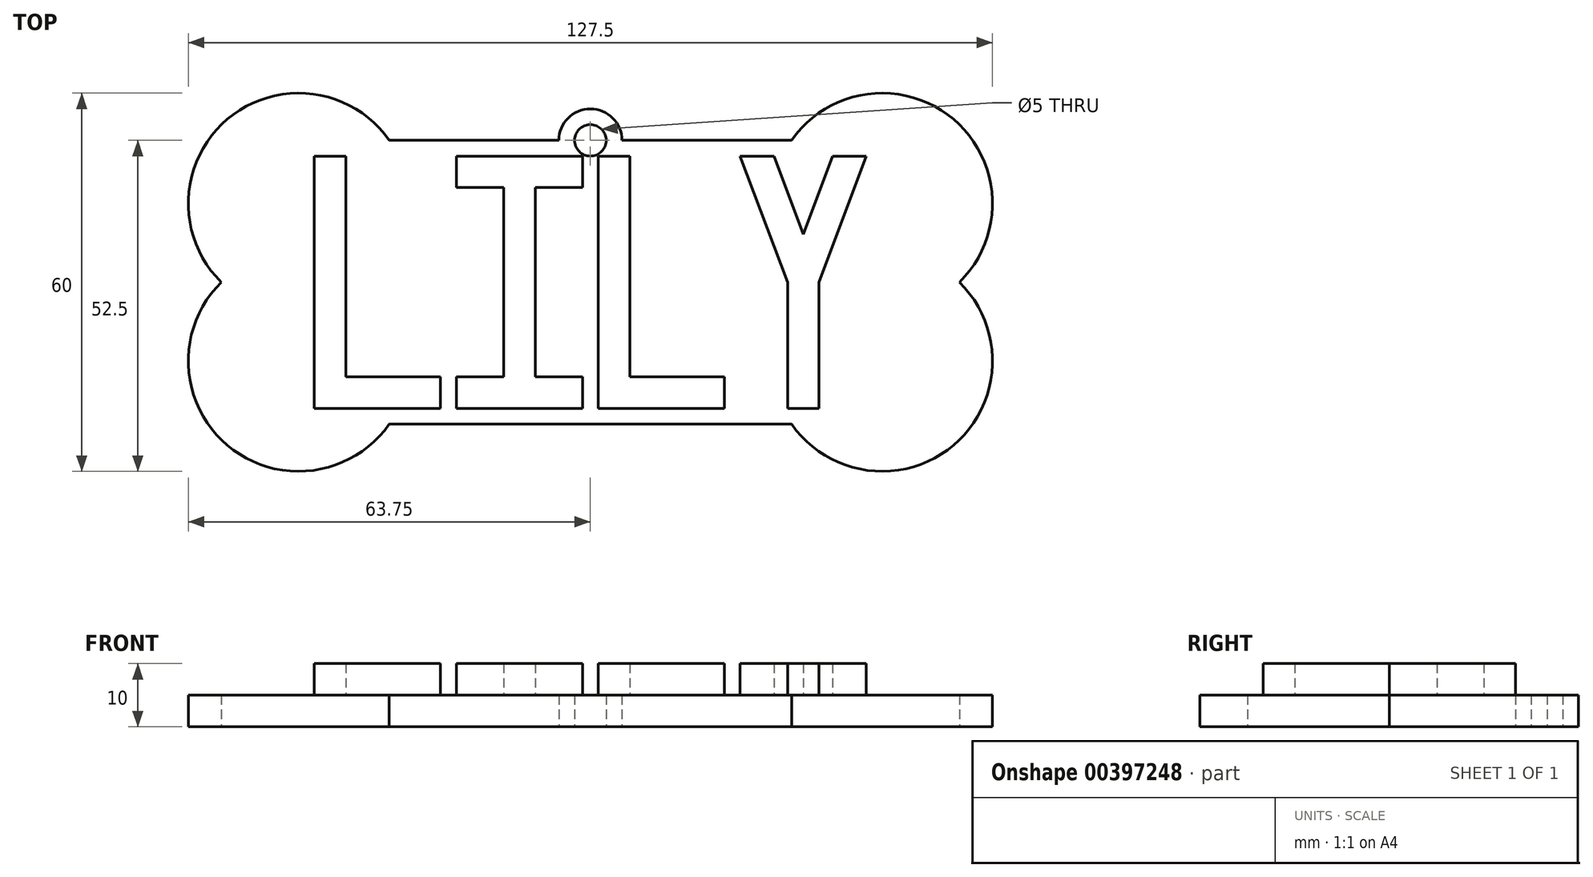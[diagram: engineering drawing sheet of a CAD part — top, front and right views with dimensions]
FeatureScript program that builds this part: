
annotation { "Feature Type Name" : "Feature", "Feature Type Description" : "" }
export const myFeature = defineFeature(function(context is Context, id is Id, definition is map)
    precondition{}
    {
        {
            var Q0;
            Q0=qCreatedBy(makeId("Top.planeOp"),FACE);
            var sketch = newSketch(context, id + "F0", { "sketchPlane" : qUnion([Q0])});
            skLineSegment(sketch, "E0.bottom", {"start": v(-90, 42.5) * mm, "end": v(-70, 42.5) * mm});
            skLineSegment(sketch, "E0.top", {"start": v(-90, 2.5) * mm, "end": v(-70, 2.5) * mm});
            skLineSegment(sketch, "E0.left", {"start": v(-90, 42.5) * mm, "end": v(-90, 2.5) * mm});
            skLineSegment(sketch, "E0.right", {"start": v(-70, 42.5) * mm, "end": v(-70, 2.5) * mm});
            skLineSegment(sketch, "E1", {"start": v(-85, 42.5) * mm, "end": v(-85, 2.5) * mm});
            skLineSegment(sketch, "E2", {"start": v(-90, 7.5) * mm, "end": v(-70, 7.5) * mm});
            skLineSegment(sketch, "E3.bottom", {"start": v(-67.5, 42.5) * mm, "end": v(-47.5, 42.5) * mm});
            skLineSegment(sketch, "E3.top", {"start": v(-67.5, 2.5) * mm, "end": v(-47.5, 2.5) * mm});
            skLineSegment(sketch, "E3.left", {"start": v(-67.5, 42.5) * mm, "end": v(-67.5, 2.5) * mm});
            skLineSegment(sketch, "E3.right", {"start": v(-47.5, 42.5) * mm, "end": v(-47.5, 2.5) * mm});
            skLineSegment(sketch, "E4.bottom", {"start": v(-22.5, 42.5) * mm, "end": v(-2.5, 42.5) * mm});
            skLineSegment(sketch, "E4.top", {"start": v(-22.5, 2.5) * mm, "end": v(-2.5, 2.5) * mm});
            skLineSegment(sketch, "E4.left", {"start": v(-22.5, 42.5) * mm, "end": v(-22.5, 2.5) * mm});
            skLineSegment(sketch, "E4.right", {"start": v(-2.5, 42.5) * mm, "end": v(-2.5, 2.5) * mm});
            skLineSegment(sketch, "E5", {"start": v(-67.5, 7.5) * mm, "end": v(-47.5, 7.5) * mm});
            skLineSegment(sketch, "E6", {"start": v(-22.5, 22.5) * mm, "end": v(-2.5, 22.5) * mm});
            skLineSegment(sketch, "E7", {"start": v(-15, 22.5) * mm, "end": v(-15, 2.5) * mm});
            skLineSegment(sketch, "E8", {"start": v(-10, 22.5) * mm, "end": v(-10, 2.5) * mm});
            skLineSegment(sketch, "E9", {"start": v(-10, 22.5) * mm, "end": v(-2.5, 42.5) * mm});
            skLineSegment(sketch, "E10", {"start": v(-15, 22.5) * mm, "end": v(-22.5, 42.5) * mm});
            skLineSegment(sketch, "E11", {"start": v(-17.16, 42.5) * mm, "end": v(-12.5, 30.07) * mm});
            skLineSegment(sketch, "E12", {"start": v(-12.5, 30.07) * mm, "end": v(-7.84, 42.5) * mm});
            skLineSegment(sketch, "E13.bottom", {"start": v(-92.5, 45) * mm, "end": v(0, 45) * mm});
            skLineSegment(sketch, "E13.top", {"start": v(-92.5, 0) * mm, "end": v(0, 0) * mm});
            skLineSegment(sketch, "E13.left", {"start": v(-92.5, 45) * mm, "end": v(-92.5, 0) * mm});
            skLineSegment(sketch, "E13.right", {"start": v(0, 45) * mm, "end": v(0, 0) * mm});
            skLineSegment(sketch, "E14", {"start": v(-67.5, 37.5) * mm, "end": v(-47.5, 37.5) * mm});
            skLineSegment(sketch, "E15", {"start": v(-60, 37.5) * mm, "end": v(-60, 7.5) * mm});
            skLineSegment(sketch, "E16", {"start": v(-55, 37.5) * mm, "end": v(-55, 7.5) * mm});
            skLineSegment(sketch, "E17.bottom", {"start": v(-45, 42.5) * mm, "end": v(-25, 42.5) * mm});
            skLineSegment(sketch, "E17.top", {"start": v(-45, 2.5) * mm, "end": v(-25, 2.5) * mm});
            skLineSegment(sketch, "E17.left", {"start": v(-45, 42.5) * mm, "end": v(-45, 2.5) * mm});
            skLineSegment(sketch, "E17.right", {"start": v(-25, 42.5) * mm, "end": v(-25, 2.5) * mm});
            skLineSegment(sketch, "E18", {"start": v(-40, 42.5) * mm, "end": v(-40, 2.5) * mm});
            skLineSegment(sketch, "E19", {"start": v(-45, 7.5) * mm, "end": v(-25, 7.5) * mm});
            skPoint(sketch, "E20", {"position": v(-92.5, 35) * mm});
            skPoint(sketch, "E21", {"position": v(-92.5, 10) * mm});
            skPoint(sketch, "E22", {"position": v(0, 10) * mm});
            skPoint(sketch, "E23", {"position": v(0, 35) * mm});
            skCircle(sketch, "E24", {"center": v(-92.5, 35) * mm, "radius": 17.5 * mm});
            skCircle(sketch, "E25", {"center": v(-92.5, 10) * mm, "radius": 17.5 * mm});
            skCircle(sketch, "E26", {"center": v(0, 35) * mm, "radius": 17.5 * mm});
            skCircle(sketch, "E27", {"center": v(0, 10) * mm, "radius": 17.5 * mm});
            skPoint(sketch, "E28", {"position": v(-46.25, 45) * mm});
            skCircle(sketch, "E29", {"center": v(-46.25, 45) * mm, "radius": 2.5 * mm});
            skCircle(sketch, "E30", {"center": v(-46.25, 45) * mm, "radius": 5 * mm});
            skSolve(sketch);
        }
        {
            var Q0;
            Q0 = qSketchRegion(id + "F0", true);
            var Q1;
            {var subQ1=sQuery(id+"F0.wireOp",EDGE,"E4.right");var subQ5=makeQuery(id+"F0.imprint","INTERSECT",VERTEX,{"derivedFrom":[subQ1,sQuery(id+"F0.wireOp",EDGE,"E6")]});Q1=makeQuery(id+"F0.imprint","IMPRINT",FACE,{"disambiguationData":[TD([[makeQuery(id+"F0.imprint","IMPRINT",EDGE,{"disambiguationData":[TD([[subQ5,1.0]])],"derivedFrom":subQ1}),1.0]])]});}
            var Q2;
            {var subQ0=sQuery(id+"F0.wireOp",EDGE,"E4.right");var subQ1=sQuery(id+"F0.wireOp",EDGE,"E4.top");var subQ2=makeQuery(id+"F0.imprint","INTERSECT",VERTEX,{"derivedFrom":[subQ1,subQ0]});Q2=makeQuery(id+"F0.imprint","IMPRINT",FACE,{"disambiguationData":[TD([[makeQuery(id+"F0.imprint","IMPRINT",EDGE,{"disambiguationData":[TD([[subQ2,1.0]])],"derivedFrom":subQ1}),1.0]])]});}
            var Q3;
            {var subQ0=sQuery(id+"F0.wireOp",EDGE,"E6");var subQ1=sQuery(id+"F0.wireOp",EDGE,"E4.right");var subQ2=makeQuery(id+"F0.imprint","INTERSECT",VERTEX,{"derivedFrom":[subQ1,subQ0]});Q3=makeQuery(id+"F0.imprint","IMPRINT",FACE,{"disambiguationData":[TD([[makeQuery(id+"F0.imprint","IMPRINT",EDGE,{"disambiguationData":[TD([[subQ2,-1.0]])],"derivedFrom":subQ1}),-1.0]])]});}
            var Q4;
            {var subQ1=sQuery(id+"F0.wireOp",EDGE,"E4.right");var subQ3=sQuery(id+"F0.wireOp",EDGE,"E27");var subQ4=makeQuery(id+"F0.imprint","INTERSECT",VERTEX,{"derivedFrom":[subQ1,subQ3]});Q4=makeQuery(id+"F0.imprint","IMPRINT",FACE,{"disambiguationData":[TD([[makeQuery(id+"F0.imprint","IMPRINT",EDGE,{"disambiguationData":[TD([[subQ4,-1.0]])],"derivedFrom":subQ3}),-1.0]])]});}
            var Q5;
            {var subQ0=sQuery(id+"F0.wireOp",EDGE,"E6");var subQ1=sQuery(id+"F0.wireOp",EDGE,"E4.right");var subQ2=makeQuery(id+"F0.imprint","INTERSECT",VERTEX,{"derivedFrom":[subQ1,subQ0]});Q5=makeQuery(id+"F0.imprint","IMPRINT",FACE,{"disambiguationData":[TD([[makeQuery(id+"F0.imprint","IMPRINT",EDGE,{"disambiguationData":[TD([[subQ2,1.0]])],"derivedFrom":subQ1}),-1.0]])]});}
            var Q6;
            {var subQ0=sQuery(id+"F0.wireOp",EDGE,"E9");var subQ3=sQuery(id+"F0.wireOp",EDGE,"E27");var subQ5=makeQuery(id+"F0.imprint","INTERSECT",VERTEX,{"derivedFrom":[subQ0,subQ3]});Q6=makeQuery(id+"F0.imprint","IMPRINT",FACE,{"disambiguationData":[TD([[makeQuery(id+"F0.imprint","IMPRINT",EDGE,{"disambiguationData":[TD([[subQ5,1.0]])],"derivedFrom":subQ0}),1.0]])]});}
            var Q7;
            {var subQ0=sQuery(id+"F0.wireOp",EDGE,"E8");var subQ3=sQuery(id+"F0.wireOp",EDGE,"E26");var subQ5=makeQuery(id+"F0.imprint","INTERSECT",VERTEX,{"derivedFrom":[subQ0,subQ3]});Q7=makeQuery(id+"F0.imprint","IMPRINT",FACE,{"disambiguationData":[TD([[makeQuery(id+"F0.imprint","IMPRINT",EDGE,{"disambiguationData":[TD([[subQ5,1.0]])],"derivedFrom":subQ0}),-1.0]])]});}
            var Q8;
            {var subQ5=sQuery(id+"F0.wireOp",EDGE,"E4.top");var subQ7=sQuery(id+"F0.wireOp",EDGE,"E7");var subQ8=makeQuery(id+"F0.imprint","INTERSECT",VERTEX,{"derivedFrom":[subQ5,subQ7]});Q8=makeQuery(id+"F0.imprint","IMPRINT",FACE,{"disambiguationData":[TD([[makeQuery(id+"F0.imprint","IMPRINT",EDGE,{"disambiguationData":[TD([[subQ8,-1.0]])],"derivedFrom":subQ5}),1.0]])]});}
            var Q9;
            {var subQ0=sQuery(id+"F0.wireOp",EDGE,"E7");var subQ3=sQuery(id+"F0.wireOp",EDGE,"E27");var subQ5=makeQuery(id+"F0.imprint","INTERSECT",VERTEX,{"derivedFrom":[subQ0,subQ3]});Q9=makeQuery(id+"F0.imprint","IMPRINT",FACE,{"disambiguationData":[TD([[makeQuery(id+"F0.imprint","IMPRINT",EDGE,{"disambiguationData":[TD([[subQ5,1.0]])],"derivedFrom":subQ0}),1.0]])]});}
            var Q10;
            {var subQ0=sQuery(id+"F0.wireOp",EDGE,"E7");var subQ1=sQuery(id+"F0.wireOp",EDGE,"E4.top");var subQ2=makeQuery(id+"F0.imprint","INTERSECT",VERTEX,{"derivedFrom":[subQ1,subQ0]});Q10=makeQuery(id+"F0.imprint","IMPRINT",FACE,{"disambiguationData":[TD([[makeQuery(id+"F0.imprint","IMPRINT",EDGE,{"disambiguationData":[TD([[subQ2,1.0]])],"derivedFrom":subQ1}),1.0]])]});}
            var Q11;
            {var subQ5=sQuery(id+"F0.wireOp",EDGE,"E4.left");var subQ7=sQuery(id+"F0.wireOp",EDGE,"E4.top");var subQ8=makeQuery(id+"F0.imprint","INTERSECT",VERTEX,{"derivedFrom":[subQ7,subQ5]});Q11=makeQuery(id+"F0.imprint","IMPRINT",FACE,{"disambiguationData":[TD([[makeQuery(id+"F0.imprint","IMPRINT",EDGE,{"disambiguationData":[TD([[subQ8,-1.0]])],"derivedFrom":subQ7}),1.0]])]});}
            var Q12;
            {var subQ0=sQuery(id+"F0.wireOp",EDGE,"E10");Q12=makeQuery(id+"F0.imprint","IMPRINT",FACE,{"disambiguationData":[TD([[makeQuery(id+"F0.imprint","IMPRINT",EDGE,{"derivedFrom":subQ0}),1.0]])]});}
            var Q13;
            {var subQ0=sQuery(id+"F0.wireOp",EDGE,"E12");Q13=makeQuery(id+"F0.imprint","IMPRINT",FACE,{"disambiguationData":[TD([[makeQuery(id+"F0.imprint","IMPRINT",EDGE,{"derivedFrom":subQ0}),-1.0]])]});}
            var Q14;
            {var subQ0=sQuery(id+"F0.wireOp",EDGE,"E10");Q14=makeQuery(id+"F0.imprint","IMPRINT",FACE,{"disambiguationData":[TD([[makeQuery(id+"F0.imprint","IMPRINT",EDGE,{"derivedFrom":subQ0}),-1.0]])]});}
            var Q15;
            {var subQ0=sQuery(id+"F0.wireOp",EDGE,"E12");Q15=makeQuery(id+"F0.imprint","IMPRINT",FACE,{"disambiguationData":[TD([[makeQuery(id+"F0.imprint","IMPRINT",EDGE,{"derivedFrom":subQ0}),1.0]])]});}
            var Q16;
            {var subQ0=sQuery(id+"F0.wireOp",EDGE,"E11");var subQ1=sQuery(id+"F0.wireOp",EDGE,"E4.bottom");var subQ2=makeQuery(id+"F0.imprint","INTERSECT",VERTEX,{"derivedFrom":[subQ1,subQ0]});Q16=makeQuery(id+"F0.imprint","IMPRINT",FACE,{"disambiguationData":[TD([[makeQuery(id+"F0.imprint","IMPRINT",EDGE,{"disambiguationData":[TD([[subQ2,-1.0]])],"derivedFrom":subQ1}),-1.0]])]});}
            var Q17;
            {var subQ0=sQuery(id+"F0.wireOp",EDGE,"E17.right");var subQ1=sQuery(id+"F0.wireOp",EDGE,"E17.bottom");var subQ2=makeQuery(id+"F0.imprint","INTERSECT",VERTEX,{"derivedFrom":[subQ1,subQ0]});Q17=makeQuery(id+"F0.imprint","IMPRINT",FACE,{"disambiguationData":[TD([[makeQuery(id+"F0.imprint","IMPRINT",EDGE,{"disambiguationData":[TD([[subQ2,1.0]])],"derivedFrom":subQ1}),-1.0]])]});}
            var Q18;
            {var subQ0=sQuery(id+"F0.wireOp",EDGE,"E17.left");var subQ1=sQuery(id+"F0.wireOp",EDGE,"E17.bottom");var subQ2=makeQuery(id+"F0.imprint","INTERSECT",VERTEX,{"derivedFrom":[subQ1,subQ0]});Q18=makeQuery(id+"F0.imprint","IMPRINT",FACE,{"disambiguationData":[TD([[makeQuery(id+"F0.imprint","IMPRINT",EDGE,{"disambiguationData":[TD([[subQ2,-1.0]])],"derivedFrom":subQ1}),-1.0]])]});}
            var Q19;
            {var subQ0=sQuery(id+"F0.wireOp",EDGE,"E17.left");var subQ1=sQuery(id+"F0.wireOp",EDGE,"E17.top");var subQ2=makeQuery(id+"F0.imprint","INTERSECT",VERTEX,{"derivedFrom":[subQ1,subQ0]});Q19=makeQuery(id+"F0.imprint","IMPRINT",FACE,{"disambiguationData":[TD([[makeQuery(id+"F0.imprint","IMPRINT",EDGE,{"disambiguationData":[TD([[subQ2,-1.0]])],"derivedFrom":subQ1}),1.0]])]});}
            var Q20;
            {var subQ0=sQuery(id+"F0.wireOp",EDGE,"E17.right");var subQ1=sQuery(id+"F0.wireOp",EDGE,"E17.top");var subQ2=makeQuery(id+"F0.imprint","INTERSECT",VERTEX,{"derivedFrom":[subQ1,subQ0]});Q20=makeQuery(id+"F0.imprint","IMPRINT",FACE,{"disambiguationData":[TD([[makeQuery(id+"F0.imprint","IMPRINT",EDGE,{"disambiguationData":[TD([[subQ2,1.0]])],"derivedFrom":subQ1}),1.0]])]});}
            var Q21;
            {var subQ5=sQuery(id+"F0.wireOp",EDGE,"E3.top");Q21=makeQuery(id+"F0.imprint","IMPRINT",FACE,{"disambiguationData":[TD([[makeQuery(id+"F0.imprint","IMPRINT",EDGE,{"derivedFrom":subQ5}),1.0]])]});}
            var Q22;
            {var subQ5=sQuery(id+"F0.wireOp",EDGE,"E16");Q22=makeQuery(id+"F0.imprint","IMPRINT",FACE,{"disambiguationData":[TD([[makeQuery(id+"F0.imprint","IMPRINT",EDGE,{"derivedFrom":subQ5}),1.0]])]});}
            var Q23;
            {var subQ0=sQuery(id+"F0.wireOp",EDGE,"E15");Q23=makeQuery(id+"F0.imprint","IMPRINT",FACE,{"disambiguationData":[TD([[makeQuery(id+"F0.imprint","IMPRINT",EDGE,{"derivedFrom":subQ0}),1.0]])]});}
            var Q24;
            {var subQ5=sQuery(id+"F0.wireOp",EDGE,"E15");Q24=makeQuery(id+"F0.imprint","IMPRINT",FACE,{"disambiguationData":[TD([[makeQuery(id+"F0.imprint","IMPRINT",EDGE,{"derivedFrom":subQ5}),-1.0]])]});}
            var Q25;
            {var subQ4=sQuery(id+"F0.wireOp",EDGE,"E3.bottom");Q25=makeQuery(id+"F0.imprint","IMPRINT",FACE,{"disambiguationData":[TD([[makeQuery(id+"F0.imprint","IMPRINT",EDGE,{"derivedFrom":subQ4}),-1.0]])]});}
            var Q26;
            {var subQ1=sQuery(id+"F0.wireOp",EDGE,"E0.bottom");var subQ6=sQuery(id+"F0.wireOp",EDGE,"E0.right");var subQ9=makeQuery(id+"F0.imprint","INTERSECT",VERTEX,{"derivedFrom":[subQ1,subQ6]});Q26=makeQuery(id+"F0.imprint","IMPRINT",FACE,{"disambiguationData":[TD([[makeQuery(id+"F0.imprint","IMPRINT",EDGE,{"disambiguationData":[TD([[subQ9,1.0]])],"derivedFrom":subQ1}),-1.0]])]});}
            var Q27;
            {var subQ0=sQuery(id+"F0.wireOp",EDGE,"E1");var subQ1=sQuery(id+"F0.wireOp",EDGE,"E0.bottom");var subQ2=makeQuery(id+"F0.imprint","INTERSECT",VERTEX,{"derivedFrom":[subQ1,subQ0]});Q27=makeQuery(id+"F0.imprint","IMPRINT",FACE,{"disambiguationData":[TD([[makeQuery(id+"F0.imprint","IMPRINT",EDGE,{"disambiguationData":[TD([[subQ2,-1.0]])],"derivedFrom":subQ1}),-1.0]])]});}
            var Q28;
            {var subQ0=sQuery(id+"F0.wireOp",EDGE,"E24");var subQ1=sQuery(id+"F0.wireOp",EDGE,"E1");var subQ2=makeQuery(id+"F0.imprint","INTERSECT",VERTEX,{"derivedFrom":[subQ1,subQ0]});Q28=makeQuery(id+"F0.imprint","IMPRINT",FACE,{"disambiguationData":[TD([[makeQuery(id+"F0.imprint","IMPRINT",EDGE,{"disambiguationData":[TD([[subQ2,-1.0]])],"derivedFrom":subQ1}),1.0]])]});}
            var Q29;
            {var subQ0=sQuery(id+"F0.wireOp",EDGE,"E25");var subQ1=sQuery(id+"F0.wireOp",EDGE,"E1");var subQ2=makeQuery(id+"F0.imprint","INTERSECT",VERTEX,{"derivedFrom":[subQ1,subQ0]});Q29=makeQuery(id+"F0.imprint","IMPRINT",FACE,{"disambiguationData":[TD([[makeQuery(id+"F0.imprint","IMPRINT",EDGE,{"disambiguationData":[TD([[subQ2,-1.0]])],"derivedFrom":subQ1}),1.0]])]});}
            var Q30;
            {var subQ0=sQuery(id+"F0.wireOp",EDGE,"E25");var subQ1=sQuery(id+"F0.wireOp",EDGE,"E0.left");var subQ2=makeQuery(id+"F0.imprint","INTERSECT",VERTEX,{"derivedFrom":[subQ1,subQ0]});Q30=makeQuery(id+"F0.imprint","IMPRINT",FACE,{"disambiguationData":[TD([[makeQuery(id+"F0.imprint","IMPRINT",EDGE,{"disambiguationData":[TD([[subQ2,-1.0]])],"derivedFrom":subQ1}),1.0]])]});}
            var Q31;
            {var subQ0=sQuery(id+"F0.wireOp",EDGE,"E0.left");var subQ1=sQuery(id+"F0.wireOp",EDGE,"E0.bottom");var subQ2=makeQuery(id+"F0.imprint","INTERSECT",VERTEX,{"derivedFrom":[subQ1,subQ0]});Q31=makeQuery(id+"F0.imprint","IMPRINT",FACE,{"disambiguationData":[TD([[makeQuery(id+"F0.imprint","IMPRINT",EDGE,{"disambiguationData":[TD([[subQ2,-1.0]])],"derivedFrom":subQ1}),-1.0]])]});}
            var Q32;
            {var subQ0=sQuery(id+"F0.wireOp",EDGE,"E25");var subQ1=sQuery(id+"F0.wireOp",EDGE,"E0.left");var subQ2=makeQuery(id+"F0.imprint","INTERSECT",VERTEX,{"derivedFrom":[subQ1,subQ0]});Q32=makeQuery(id+"F0.imprint","IMPRINT",FACE,{"disambiguationData":[TD([[makeQuery(id+"F0.imprint","IMPRINT",EDGE,{"disambiguationData":[TD([[subQ2,-1.0]])],"derivedFrom":subQ1}),-1.0]])]});}
            var Q33;
            {var subQ0=sQuery(id+"F0.wireOp",EDGE,"E2");var subQ1=sQuery(id+"F0.wireOp",EDGE,"E0.left");var subQ2=makeQuery(id+"F0.imprint","INTERSECT",VERTEX,{"derivedFrom":[subQ1,subQ0]});Q33=makeQuery(id+"F0.imprint","IMPRINT",FACE,{"disambiguationData":[TD([[makeQuery(id+"F0.imprint","IMPRINT",EDGE,{"disambiguationData":[TD([[subQ2,1.0]])],"derivedFrom":subQ1}),1.0]])]});}
            var Q34;
            {var subQ0=sQuery(id+"F0.wireOp",EDGE,"E0.left");var subQ1=sQuery(id+"F0.wireOp",EDGE,"E0.top");var subQ2=makeQuery(id+"F0.imprint","INTERSECT",VERTEX,{"derivedFrom":[subQ1,subQ0]});Q34=makeQuery(id+"F0.imprint","IMPRINT",FACE,{"disambiguationData":[TD([[makeQuery(id+"F0.imprint","IMPRINT",EDGE,{"disambiguationData":[TD([[subQ2,-1.0]])],"derivedFrom":subQ1}),1.0]])]});}
            var Q35;
            {var subQ0=sQuery(id+"F0.wireOp",EDGE,"E1");var subQ1=sQuery(id+"F0.wireOp",EDGE,"E0.top");var subQ2=makeQuery(id+"F0.imprint","INTERSECT",VERTEX,{"derivedFrom":[subQ1,subQ0]});Q35=makeQuery(id+"F0.imprint","IMPRINT",FACE,{"disambiguationData":[TD([[makeQuery(id+"F0.imprint","IMPRINT",EDGE,{"disambiguationData":[TD([[subQ2,-1.0]])],"derivedFrom":subQ1}),1.0]])]});}
            var Q36;
            {var subQ0=sQuery(id+"F0.wireOp",EDGE,"E0.right");var subQ1=sQuery(id+"F0.wireOp",EDGE,"E0.top");var subQ2=makeQuery(id+"F0.imprint","INTERSECT",VERTEX,{"derivedFrom":[subQ1,subQ0]});Q36=makeQuery(id+"F0.imprint","IMPRINT",FACE,{"disambiguationData":[TD([[makeQuery(id+"F0.imprint","IMPRINT",EDGE,{"disambiguationData":[TD([[subQ2,1.0]])],"derivedFrom":subQ1}),1.0]])]});}
            extrude(context, id + "F1", {"entities" : qUnion([Q0, Q1, Q2, Q3, Q4, Q5, Q6, Q7, Q8, Q9, Q10, Q11, Q12, Q13, Q14, Q15, Q16, Q17, Q18, Q19, Q20, Q21, Q22, Q23, Q24, Q25, Q26, Q27, Q28, Q29, Q30, Q31, Q32, Q33, Q34, Q35, Q36]), "depth" : 5 * mm});
        }
        {
            var Q0;
            {var subQ0=sQuery(id+"F0.wireOp",EDGE,"E0.left");var subQ1=sQuery(id+"F0.wireOp",EDGE,"E0.bottom");var subQ2=makeQuery(id+"F0.imprint","INTERSECT",VERTEX,{"derivedFrom":[subQ1,subQ0]});Q0=makeQuery(id+"F0.imprint","IMPRINT",FACE,{"disambiguationData":[TD([[makeQuery(id+"F0.imprint","IMPRINT",EDGE,{"disambiguationData":[TD([[subQ2,-1.0]])],"derivedFrom":subQ1}),-1.0]])]});}
            var Q1;
            {var subQ0=sQuery(id+"F0.wireOp",EDGE,"E25");var subQ1=sQuery(id+"F0.wireOp",EDGE,"E0.left");var subQ2=makeQuery(id+"F0.imprint","INTERSECT",VERTEX,{"derivedFrom":[subQ1,subQ0]});Q1=makeQuery(id+"F0.imprint","IMPRINT",FACE,{"disambiguationData":[TD([[makeQuery(id+"F0.imprint","IMPRINT",EDGE,{"disambiguationData":[TD([[subQ2,-1.0]])],"derivedFrom":subQ1}),1.0]])]});}
            var Q2;
            {var subQ0=sQuery(id+"F0.wireOp",EDGE,"E2");var subQ1=sQuery(id+"F0.wireOp",EDGE,"E0.left");var subQ2=makeQuery(id+"F0.imprint","INTERSECT",VERTEX,{"derivedFrom":[subQ1,subQ0]});Q2=makeQuery(id+"F0.imprint","IMPRINT",FACE,{"disambiguationData":[TD([[makeQuery(id+"F0.imprint","IMPRINT",EDGE,{"disambiguationData":[TD([[subQ2,1.0]])],"derivedFrom":subQ1}),1.0]])]});}
            var Q3;
            {var subQ0=sQuery(id+"F0.wireOp",EDGE,"E0.left");var subQ1=sQuery(id+"F0.wireOp",EDGE,"E0.top");var subQ2=makeQuery(id+"F0.imprint","INTERSECT",VERTEX,{"derivedFrom":[subQ1,subQ0]});Q3=makeQuery(id+"F0.imprint","IMPRINT",FACE,{"disambiguationData":[TD([[makeQuery(id+"F0.imprint","IMPRINT",EDGE,{"disambiguationData":[TD([[subQ2,-1.0]])],"derivedFrom":subQ1}),1.0]])]});}
            var Q4;
            {var subQ0=sQuery(id+"F0.wireOp",EDGE,"E1");var subQ1=sQuery(id+"F0.wireOp",EDGE,"E0.top");var subQ2=makeQuery(id+"F0.imprint","INTERSECT",VERTEX,{"derivedFrom":[subQ1,subQ0]});Q4=makeQuery(id+"F0.imprint","IMPRINT",FACE,{"disambiguationData":[TD([[makeQuery(id+"F0.imprint","IMPRINT",EDGE,{"disambiguationData":[TD([[subQ2,-1.0]])],"derivedFrom":subQ1}),1.0]])]});}
            var Q5;
            {var subQ0=sQuery(id+"F0.wireOp",EDGE,"E0.right");var subQ1=sQuery(id+"F0.wireOp",EDGE,"E0.top");var subQ2=makeQuery(id+"F0.imprint","INTERSECT",VERTEX,{"derivedFrom":[subQ1,subQ0]});Q5=makeQuery(id+"F0.imprint","IMPRINT",FACE,{"disambiguationData":[TD([[makeQuery(id+"F0.imprint","IMPRINT",EDGE,{"disambiguationData":[TD([[subQ2,1.0]])],"derivedFrom":subQ1}),1.0]])]});}
            var Q6;
            {var subQ0=sQuery(id+"F0.wireOp",EDGE,"E15");Q6=makeQuery(id+"F0.imprint","IMPRINT",FACE,{"disambiguationData":[TD([[makeQuery(id+"F0.imprint","IMPRINT",EDGE,{"derivedFrom":subQ0}),1.0]])]});}
            var Q7;
            {var subQ4=sQuery(id+"F0.wireOp",EDGE,"E3.bottom");Q7=makeQuery(id+"F0.imprint","IMPRINT",FACE,{"disambiguationData":[TD([[makeQuery(id+"F0.imprint","IMPRINT",EDGE,{"derivedFrom":subQ4}),-1.0]])]});}
            var Q8;
            {var subQ5=sQuery(id+"F0.wireOp",EDGE,"E3.top");Q8=makeQuery(id+"F0.imprint","IMPRINT",FACE,{"disambiguationData":[TD([[makeQuery(id+"F0.imprint","IMPRINT",EDGE,{"derivedFrom":subQ5}),1.0]])]});}
            var Q9;
            {var subQ0=sQuery(id+"F0.wireOp",EDGE,"E17.left");var subQ1=sQuery(id+"F0.wireOp",EDGE,"E17.bottom");var subQ2=makeQuery(id+"F0.imprint","INTERSECT",VERTEX,{"derivedFrom":[subQ1,subQ0]});Q9=makeQuery(id+"F0.imprint","IMPRINT",FACE,{"disambiguationData":[TD([[makeQuery(id+"F0.imprint","IMPRINT",EDGE,{"disambiguationData":[TD([[subQ2,-1.0]])],"derivedFrom":subQ1}),-1.0]])]});}
            var Q10;
            {var subQ0=sQuery(id+"F0.wireOp",EDGE,"E17.left");var subQ1=sQuery(id+"F0.wireOp",EDGE,"E17.top");var subQ2=makeQuery(id+"F0.imprint","INTERSECT",VERTEX,{"derivedFrom":[subQ1,subQ0]});Q10=makeQuery(id+"F0.imprint","IMPRINT",FACE,{"disambiguationData":[TD([[makeQuery(id+"F0.imprint","IMPRINT",EDGE,{"disambiguationData":[TD([[subQ2,-1.0]])],"derivedFrom":subQ1}),1.0]])]});}
            var Q11;
            {var subQ0=sQuery(id+"F0.wireOp",EDGE,"E17.right");var subQ1=sQuery(id+"F0.wireOp",EDGE,"E17.top");var subQ2=makeQuery(id+"F0.imprint","INTERSECT",VERTEX,{"derivedFrom":[subQ1,subQ0]});Q11=makeQuery(id+"F0.imprint","IMPRINT",FACE,{"disambiguationData":[TD([[makeQuery(id+"F0.imprint","IMPRINT",EDGE,{"disambiguationData":[TD([[subQ2,1.0]])],"derivedFrom":subQ1}),1.0]])]});}
            var Q12;
            {var subQ5=sQuery(id+"F0.wireOp",EDGE,"E4.top");var subQ7=sQuery(id+"F0.wireOp",EDGE,"E7");var subQ8=makeQuery(id+"F0.imprint","INTERSECT",VERTEX,{"derivedFrom":[subQ5,subQ7]});Q12=makeQuery(id+"F0.imprint","IMPRINT",FACE,{"disambiguationData":[TD([[makeQuery(id+"F0.imprint","IMPRINT",EDGE,{"disambiguationData":[TD([[subQ8,-1.0]])],"derivedFrom":subQ5}),1.0]])]});}
            var Q13;
            {var subQ0=sQuery(id+"F0.wireOp",EDGE,"E12");Q13=makeQuery(id+"F0.imprint","IMPRINT",FACE,{"disambiguationData":[TD([[makeQuery(id+"F0.imprint","IMPRINT",EDGE,{"derivedFrom":subQ0}),-1.0]])]});}
            var Q14;
            {var subQ0=sQuery(id+"F0.wireOp",EDGE,"E10");Q14=makeQuery(id+"F0.imprint","IMPRINT",FACE,{"disambiguationData":[TD([[makeQuery(id+"F0.imprint","IMPRINT",EDGE,{"derivedFrom":subQ0}),-1.0]])]});}
            var Q15;
            {var subQ0=sQuery(id+"F0.wireOp",EDGE,"E7");var subQ3=sQuery(id+"F0.wireOp",EDGE,"E27");var subQ5=makeQuery(id+"F0.imprint","INTERSECT",VERTEX,{"derivedFrom":[subQ0,subQ3]});Q15=makeQuery(id+"F0.imprint","IMPRINT",FACE,{"disambiguationData":[TD([[makeQuery(id+"F0.imprint","IMPRINT",EDGE,{"disambiguationData":[TD([[subQ5,1.0]])],"derivedFrom":subQ0}),1.0]])]});}
            var Q16;
            {var subQ0=sQuery(id+"F0.wireOp",EDGE,"E8");var subQ3=sQuery(id+"F0.wireOp",EDGE,"E26");var subQ5=makeQuery(id+"F0.imprint","INTERSECT",VERTEX,{"derivedFrom":[subQ0,subQ3]});Q16=makeQuery(id+"F0.imprint","IMPRINT",FACE,{"disambiguationData":[TD([[makeQuery(id+"F0.imprint","IMPRINT",EDGE,{"disambiguationData":[TD([[subQ5,1.0]])],"derivedFrom":subQ0}),-1.0]])]});}
            var Q17;
            {var subQ0=sQuery(id+"F0.wireOp",EDGE,"E9");var subQ3=sQuery(id+"F0.wireOp",EDGE,"E27");var subQ5=makeQuery(id+"F0.imprint","INTERSECT",VERTEX,{"derivedFrom":[subQ0,subQ3]});Q17=makeQuery(id+"F0.imprint","IMPRINT",FACE,{"disambiguationData":[TD([[makeQuery(id+"F0.imprint","IMPRINT",EDGE,{"disambiguationData":[TD([[subQ5,1.0]])],"derivedFrom":subQ0}),1.0]])]});}
            var Q18;
            {var subQ1=sQuery(id+"F0.wireOp",EDGE,"E3.left");var subQ8=sQuery(id+"F0.wireOp",EDGE,"E3.bottom");var subQ9=makeQuery(id+"F0.imprint","INTERSECT",VERTEX,{"derivedFrom":[subQ8,subQ1]});Q18=makeQuery(id+"F0.imprint","IMPRINT",FACE,{"disambiguationData":[TD([[makeQuery(id+"F0.imprint","IMPRINT",EDGE,{"disambiguationData":[TD([[subQ9,-1.0]])],"derivedFrom":subQ8}),-1.0]])]});}
            var Q19;
            {var subQ3=sQuery(id+"F0.wireOp",EDGE,"E18");var subQ5=sQuery(id+"F0.wireOp",EDGE,"E17.bottom");var subQ6=makeQuery(id+"F0.imprint","INTERSECT",VERTEX,{"derivedFrom":[subQ5,subQ3]});Q19=makeQuery(id+"F0.imprint","IMPRINT",FACE,{"disambiguationData":[TD([[makeQuery(id+"F0.imprint","IMPRINT",EDGE,{"disambiguationData":[TD([[subQ6,1.0]])],"derivedFrom":subQ5}),-1.0]])]});}
            extrude(context, id + "F2", {"entities" : qUnion([Q0, Q1, Q2, Q3, Q4, Q5, Q6, Q7, Q8, Q9, Q10, Q11, Q12, Q13, Q14, Q15, Q16, Q17, Q18, Q19]), "operationType" : NewBodyOperationType.ADD, "depth" : 10 * mm});
        }
    });
